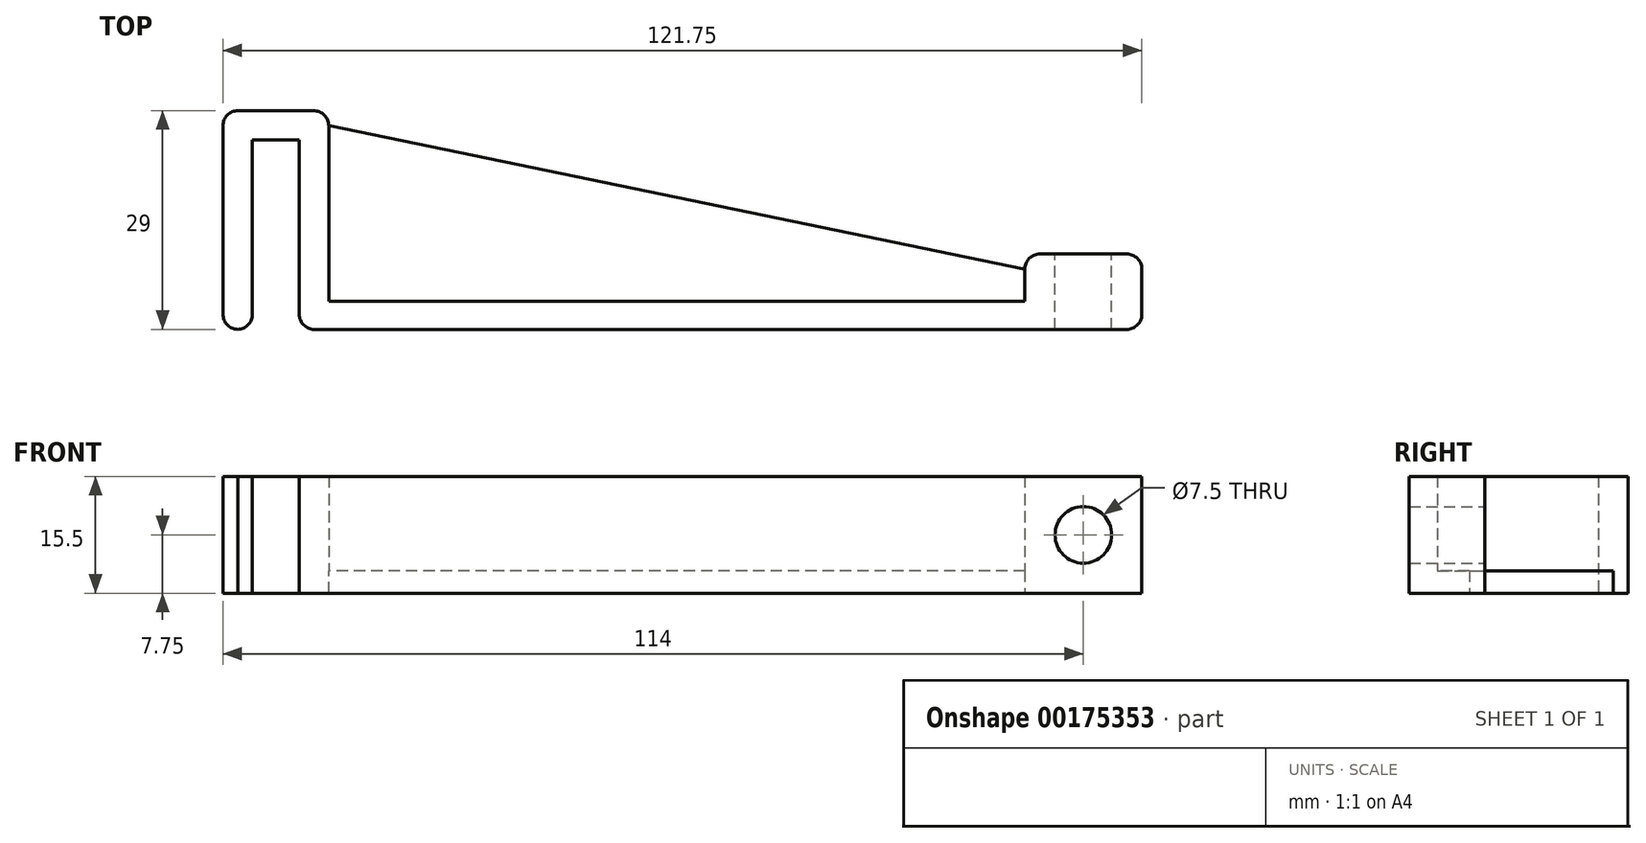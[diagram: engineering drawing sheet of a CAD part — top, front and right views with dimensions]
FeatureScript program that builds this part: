
annotation { "Feature Type Name" : "Feature", "Feature Type Description" : "" }
export const myFeature = defineFeature(function(context is Context, id is Id, definition is map)
    precondition{}
    {
        {
            var Q0;
            Q0=qCreatedBy(makeId("Top.planeOp"),FACE);
            var sketch = newSketch(context, id + "F0", { "sketchPlane" : qUnion([Q0])});
            skLineSegment(sketch, "E0.bottom", {"start": v(7, -14.5) * mm, "end": v(3.1, -14.5) * mm});
            skLineSegment(sketch, "E0.top", {"start": v(7, 14.5) * mm, "end": v(-7, 14.5) * mm});
            skLineSegment(sketch, "E0.left", {"start": v(7, -10.75) * mm, "end": v(7, 14.5) * mm});
            skLineSegment(sketch, "E0.right", {"start": v(-7, -14.5) * mm, "end": v(-7, 14.5) * mm});
            skPoint(sketch, "E0.middle", {"position": v(0, 0) * mm});
            skLineSegment(sketch, "E1", {"start": v(7, -14.5) * mm, "end": v(114.75, -14.5) * mm});
            skLineSegment(sketch, "E2", {"start": v(114.75, -14.5) * mm, "end": v(114.75, -4.5) * mm});
            skLineSegment(sketch, "E3", {"start": v(114.75, -4.5) * mm, "end": v(99.25, -4.5) * mm});
            skLineSegment(sketch, "E4", {"start": v(99.25, -4.5) * mm, "end": v(99.25, -10.75) * mm});
            skLineSegment(sketch, "E5", {"start": v(99.25, -10.75) * mm, "end": v(7, -10.75) * mm});
            skLineSegment(sketch, "E6.0", {"start": v(-3.1, -14.5) * mm, "end": v(-3.1, 10.6) * mm});
            skLineSegment(sketch, "E6.1", {"start": v(3.1, 10.6) * mm, "end": v(-3.1, 10.6) * mm});
            skLineSegment(sketch, "E6.2", {"start": v(3.1, -14.5) * mm, "end": v(3.1, 10.6) * mm});
            skLineSegment(sketch, "E7.trimOffspring", {"start": v(-3.1, -14.5) * mm, "end": v(-7, -14.5) * mm});
            skSolve(sketch);
        }
        {
            var Q0;
            Q0=makeQuery(id+"F0.imprint","IMPRINT",FACE,{"disambiguationData":[TD([[makeQuery(id+"F0.imprint","IMPRINT",EDGE,{"derivedFrom":sQuery(id+"F0.wireOp",EDGE,"E0.bottom")}),-1.0]])]});
            extrude(context, id + "F1", {"entities" : qUnion([Q0]), "depth" : 15.5 * mm});
        }
        {
            var Q0;
            Q0=makeQuery(id+"F1.opExtrude","SWEPT_FACE",FACE,{"disambiguationData":[OSD([sQuery(id+"F0.wireOp",EDGE,"E3")])]});
            var sketch = newSketch(context, id + "F2", { "sketchPlane" : qUnion([Q0])});
            skCircle(sketch, "E8", {"center": v(-107, 7.75) * mm, "radius": 3.75 * mm});
            skPoint(sketch, "E8.centerSnap0", {"position": v(-114.75, 7.75) * mm});
            skPoint(sketch, "E8.centerSnap1", {"position": v(-107, 0) * mm});
            skSolve(sketch);
        }
        {
            var Q0;
            Q0 = qSketchRegion(id + "F2", true);
            extrude(context, id + "F3", {"entities" : qUnion([Q0]), "operationType" : NewBodyOperationType.REMOVE, "endBound" : BoundingType.UP_TO_NEXT, "oppositeDirection" : true, "depth" : 25 * mm});
        }
        {
            var Q0;
            Q0=makeQuery(id+"F1.opExtrude","SWEPT_EDGE",EDGE,{"disambiguationData":[OSD([sQuery(id+"F0.wireOp",EDGE,"E0.top"),sQuery(id+"F0.wireOp",EDGE,"E0.right")])]});
            var Q1;
            Q1=makeQuery(id+"F1.opExtrude","SWEPT_EDGE",EDGE,{"disambiguationData":[OSD([sQuery(id+"F0.wireOp",EDGE,"E0.top"),sQuery(id+"F0.wireOp",EDGE,"E0.left")])]});
            var Q2;
            Q2=makeQuery(id+"F1.opExtrude","SWEPT_EDGE",EDGE,{"disambiguationData":[OSD([sQuery(id+"F0.wireOp",EDGE,"E3"),sQuery(id+"F0.wireOp",EDGE,"E4")])]});
            var Q3;
            Q3=makeQuery(id+"F1.opExtrude","SWEPT_EDGE",EDGE,{"disambiguationData":[OSD([sQuery(id+"F0.wireOp",EDGE,"E2"),sQuery(id+"F0.wireOp",EDGE,"E3")])]});
            var Q4;
            Q4=makeQuery(id+"F1.opExtrude","SWEPT_EDGE",EDGE,{"disambiguationData":[OSD([sQuery(id+"F0.wireOp",EDGE,"E1"),sQuery(id+"F0.wireOp",EDGE,"E2")])]});
            var Q5;
            Q5=makeQuery(id+"F1.opExtrude","SWEPT_EDGE",EDGE,{"disambiguationData":[OSD([sQuery(id+"F0.wireOp",EDGE,"E0.bottom"),sQuery(id+"F0.wireOp",EDGE,"E6.2")])]});
            var Q6;
            Q6=makeQuery(id+"F1.opExtrude","SWEPT_EDGE",EDGE,{"disambiguationData":[OSD([sQuery(id+"F0.wireOp",EDGE,"E6.0"),sQuery(id+"F0.wireOp",EDGE,"E7.trimOffspring")])]});
            var Q7;
            Q7=makeQuery(id+"F1.opExtrude","SWEPT_EDGE",EDGE,{"disambiguationData":[OSD([sQuery(id+"F0.wireOp",EDGE,"E0.right"),sQuery(id+"F0.wireOp",EDGE,"E7.trimOffspring")])]});
            fillet(context, id + "F4", {"entities" : qUnion([Q0, Q1, Q2, Q3, Q4, Q5, Q6, Q7]), "radius" : 2 * mm, "tangentPropagation" : true, "allowEdgeOverflow" : false});
        }
        {
            var Q0;
            Q0=makeQuery(id+"F1.opExtrude","SWEPT_FACE",FACE,{"disambiguationData":[OSD([sQuery(id+"F0.wireOp",EDGE,"E5")])]});
            var sketch = newSketch(context, id + "F5", { "sketchPlane" : qUnion([Q0])});
            skLineSegment(sketch, "E9.bottom", {"start": v(-99.25, 0) * mm, "end": v(-7, 0) * mm});
            skLineSegment(sketch, "E9.top", {"start": v(-99.25, 3) * mm, "end": v(-7, 3) * mm});
            skLineSegment(sketch, "E9.left", {"start": v(-99.25, 0) * mm, "end": v(-99.25, 3) * mm});
            skLineSegment(sketch, "E9.right", {"start": v(-7, 0) * mm, "end": v(-7, 3) * mm});
            skSolve(sketch);
        }
        {
            var Q0;
            Q0=makeQuery(id+"F5.imprint","IMPRINT",FACE,{"disambiguationData":[TD([[makeQuery(id+"F5.imprint","IMPRINT",EDGE,{"derivedFrom":sQuery(id+"F5.wireOp",EDGE,"E9.bottom")}),1.0]])]});
            extrude(context, id + "F6", {"entities" : qUnion([Q0]), "operationType" : NewBodyOperationType.ADD, "depth" : 23.3 * mm});
        }
        {
            var Q0;
            Q0=makeQuery(id+"F6.boolean.opBoolean","MERGE",FACE,{"derivedFrom":[makeQuery(id+"F1.opExtrude","CAP_FACE",FACE,{"disambiguationData":[OSD([sQuery(id+"F0.wireOp",EDGE,"E0.bottom"),sQuery(id+"F0.wireOp",EDGE,"E0.top"),sQuery(id+"F0.wireOp",EDGE,"E0.left"),sQuery(id+"F0.wireOp",EDGE,"E0.right"),sQuery(id+"F0.wireOp",EDGE,"E1"),sQuery(id+"F0.wireOp",EDGE,"E2"),sQuery(id+"F0.wireOp",EDGE,"E3"),sQuery(id+"F0.wireOp",EDGE,"E4"),sQuery(id+"F0.wireOp",EDGE,"E5"),sQuery(id+"F0.wireOp",EDGE,"E6.0"),sQuery(id+"F0.wireOp",EDGE,"E6.1"),sQuery(id+"F0.wireOp",EDGE,"E6.2"),sQuery(id+"F0.wireOp",EDGE,"E7.trimOffspring")])],"isStart":true}),makeQuery(id+"F6.opExtrude","SWEPT_FACE",FACE,{"disambiguationData":[OSD([sQuery(id+"F5.wireOp",EDGE,"E9.bottom")])]})]});
            var sketch = newSketch(context, id + "F7", { "sketchPlane" : qUnion([Q0])});
            skLineSegment(sketch, "E10", {"start": v(99.25, 6.5) * mm, "end": v(7, -12.55) * mm});
            skLineSegment(sketch, "E11", {"start": v(7, -12.55) * mm, "end": v(99.25, -12.55) * mm});
            skLineSegment(sketch, "E12", {"start": v(99.25, -12.55) * mm, "end": v(99.25, 6.5) * mm});
            skSolve(sketch);
        }
        {
            var Q0;
            Q0=makeQuery(id+"F7.imprint","IMPRINT",FACE,{"disambiguationData":[TD([[makeQuery(id+"F7.imprint","IMPRINT",EDGE,{"derivedFrom":sQuery(id+"F7.wireOp",EDGE,"E10")}),1.0]])]});
            extrude(context, id + "F8", {"entities" : qUnion([Q0]), "operationType" : NewBodyOperationType.REMOVE, "endBound" : BoundingType.UP_TO_NEXT, "oppositeDirection" : true, "depth" : 25 * mm});
        }
    });
